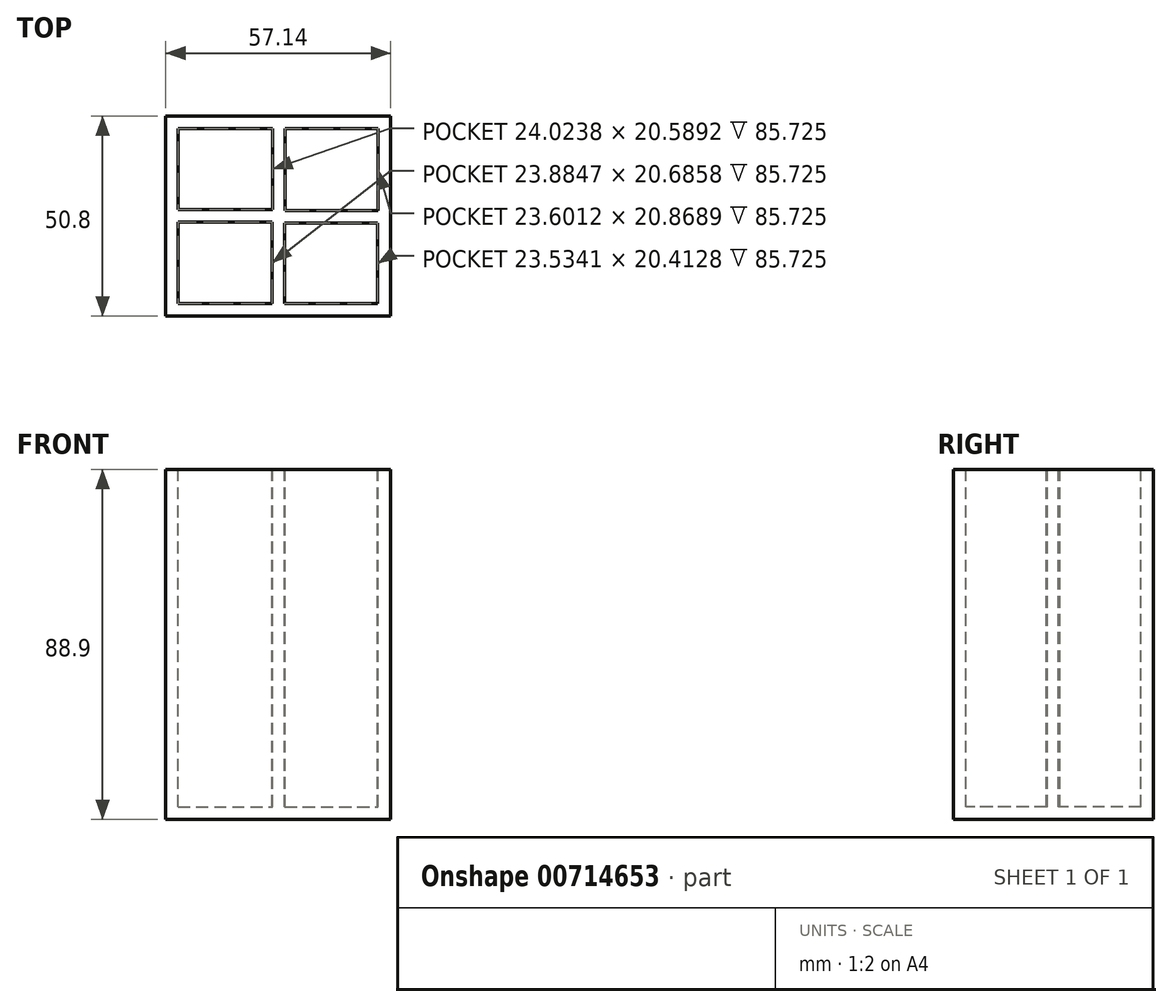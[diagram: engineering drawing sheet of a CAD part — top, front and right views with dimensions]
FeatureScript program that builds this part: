
annotation { "Feature Type Name" : "Feature", "Feature Type Description" : "" }
export const myFeature = defineFeature(function(context is Context, id is Id, definition is map)
    precondition{}
    {
        {
            var Q0;
            Q0=qCreatedBy(makeId("Top.planeOp"),FACE);
            var sketch = newSketch(context, id + "F0", { "sketchPlane" : qUnion([Q0])});
            skLineSegment(sketch, "E0.bottom", {"start": v(28.57, 25.4) * mm, "end": v(-28.57, 25.4) * mm});
            skLineSegment(sketch, "E0.top", {"start": v(28.57, -25.4) * mm, "end": v(-28.57, -25.4) * mm});
            skLineSegment(sketch, "E0.left", {"start": v(28.58, 25.4) * mm, "end": v(28.57, -25.4) * mm});
            skLineSegment(sketch, "E0.right", {"start": v(-28.57, 25.4) * mm, "end": v(-28.57, -25.4) * mm});
            skPoint(sketch, "E0.middle", {"position": v(0, 0) * mm});
            skSolve(sketch);
        }
        {
            var Q0;
            Q0=makeQuery(id+"F0.imprint","IMPRINT",FACE,{"disambiguationData":[TD([[makeQuery(id+"F0.imprint","IMPRINT",EDGE,{"derivedFrom":sQuery(id+"F0.wireOp",EDGE,"E0.bottom")}),1.0]])]});
            extrude(context, id + "F1", {"entities" : qUnion([Q0]), "depth" : 88.9 * mm, "offsetDistance" : 25.4 * mm});
        }
        {
            var Q0;
            Q0=makeQuery(id+"F1.opExtrude","CAP_FACE",FACE,{"disambiguationData":[OSD([sQuery(id+"F0.wireOp",EDGE,"E0.bottom"),sQuery(id+"F0.wireOp",EDGE,"E0.top"),sQuery(id+"F0.wireOp",EDGE,"E0.left"),sQuery(id+"F0.wireOp",EDGE,"E0.right")])],"isStart":false});
            var sketch = newSketch(context, id + "F2", { "sketchPlane" : qUnion([Q0])});
            skLineSegment(sketch, "E1.bottom", {"start": v(-25.4, 22.23) * mm, "end": v(-1.38, 22.23) * mm});
            skLineSegment(sketch, "E1.top", {"start": v(-25.4, 1.64) * mm, "end": v(-1.38, 1.64) * mm});
            skLineSegment(sketch, "E1.left", {"start": v(-25.4, 22.23) * mm, "end": v(-25.4, 1.64) * mm});
            skLineSegment(sketch, "E1.right", {"start": v(-1.38, 22.23) * mm, "end": v(-1.38, 1.64) * mm});
            skLineSegment(sketch, "E2.bottom", {"start": v(1.8, 22.23) * mm, "end": v(25.4, 22.23) * mm});
            skLineSegment(sketch, "E2.top", {"start": v(1.8, 1.36) * mm, "end": v(25.4, 1.36) * mm});
            skLineSegment(sketch, "E2.left", {"start": v(1.8, 22.23) * mm, "end": v(1.8, 1.36) * mm});
            skLineSegment(sketch, "E2.right", {"start": v(25.4, 22.22) * mm, "end": v(25.4, 1.36) * mm});
            skLineSegment(sketch, "E3.bottom", {"start": v(1.66, -1.81) * mm, "end": v(25.2, -1.81) * mm});
            skLineSegment(sketch, "E3.top", {"start": v(1.66, -22.23) * mm, "end": v(25.2, -22.23) * mm});
            skLineSegment(sketch, "E3.left", {"start": v(1.66, -1.81) * mm, "end": v(1.66, -22.23) * mm});
            skLineSegment(sketch, "E3.right", {"start": v(25.2, -1.81) * mm, "end": v(25.2, -22.23) * mm});
            skLineSegment(sketch, "E4.bottom", {"start": v(-25.4, -1.54) * mm, "end": v(-1.52, -1.54) * mm});
            skLineSegment(sketch, "E4.top", {"start": v(-25.4, -22.23) * mm, "end": v(-1.52, -22.23) * mm});
            skLineSegment(sketch, "E4.left", {"start": v(-25.4, -1.54) * mm, "end": v(-25.4, -22.23) * mm});
            skLineSegment(sketch, "E4.right", {"start": v(-1.52, -1.54) * mm, "end": v(-1.52, -22.23) * mm});
            skSolve(sketch);
        }
        {
            var Q0;
            Q0=makeQuery(id+"F2.imprint","IMPRINT",FACE,{"disambiguationData":[TD([[makeQuery(id+"F2.imprint","IMPRINT",EDGE,{"derivedFrom":sQuery(id+"F2.wireOp",EDGE,"E1.bottom")}),-1.0]])]});
            extrude(context, id + "F3", {"entities" : qUnion([Q0]), "operationType" : NewBodyOperationType.REMOVE, "oppositeDirection" : true, "depth" : 85.72 * mm, "offsetDistance" : 25.4 * mm});
        }
        {
            var Q0;
            Q0=makeQuery(id+"F2.imprint","IMPRINT",FACE,{"disambiguationData":[TD([[makeQuery(id+"F2.imprint","IMPRINT",EDGE,{"derivedFrom":sQuery(id+"F2.wireOp",EDGE,"E4.bottom")}),-1.0]])]});
            extrude(context, id + "F4", {"entities" : qUnion([Q0]), "operationType" : NewBodyOperationType.REMOVE, "oppositeDirection" : true, "depth" : 85.72 * mm, "offsetDistance" : 25.4 * mm});
        }
        {
            var Q0;
            Q0=makeQuery(id+"F2.imprint","IMPRINT",FACE,{"disambiguationData":[TD([[makeQuery(id+"F2.imprint","IMPRINT",EDGE,{"derivedFrom":sQuery(id+"F2.wireOp",EDGE,"E2.bottom")}),-1.0]])]});
            extrude(context, id + "F5", {"entities" : qUnion([Q0]), "operationType" : NewBodyOperationType.REMOVE, "oppositeDirection" : true, "depth" : 85.72 * mm, "offsetDistance" : 25.4 * mm});
        }
        {
            var Q0;
            Q0=makeQuery(id+"F2.imprint","IMPRINT",FACE,{"disambiguationData":[TD([[makeQuery(id+"F2.imprint","IMPRINT",EDGE,{"derivedFrom":sQuery(id+"F2.wireOp",EDGE,"E3.bottom")}),-1.0]])]});
            extrude(context, id + "F6", {"entities" : qUnion([Q0]), "operationType" : NewBodyOperationType.REMOVE, "oppositeDirection" : true, "depth" : 85.72 * mm, "offsetDistance" : 25.4 * mm});
        }
    });
